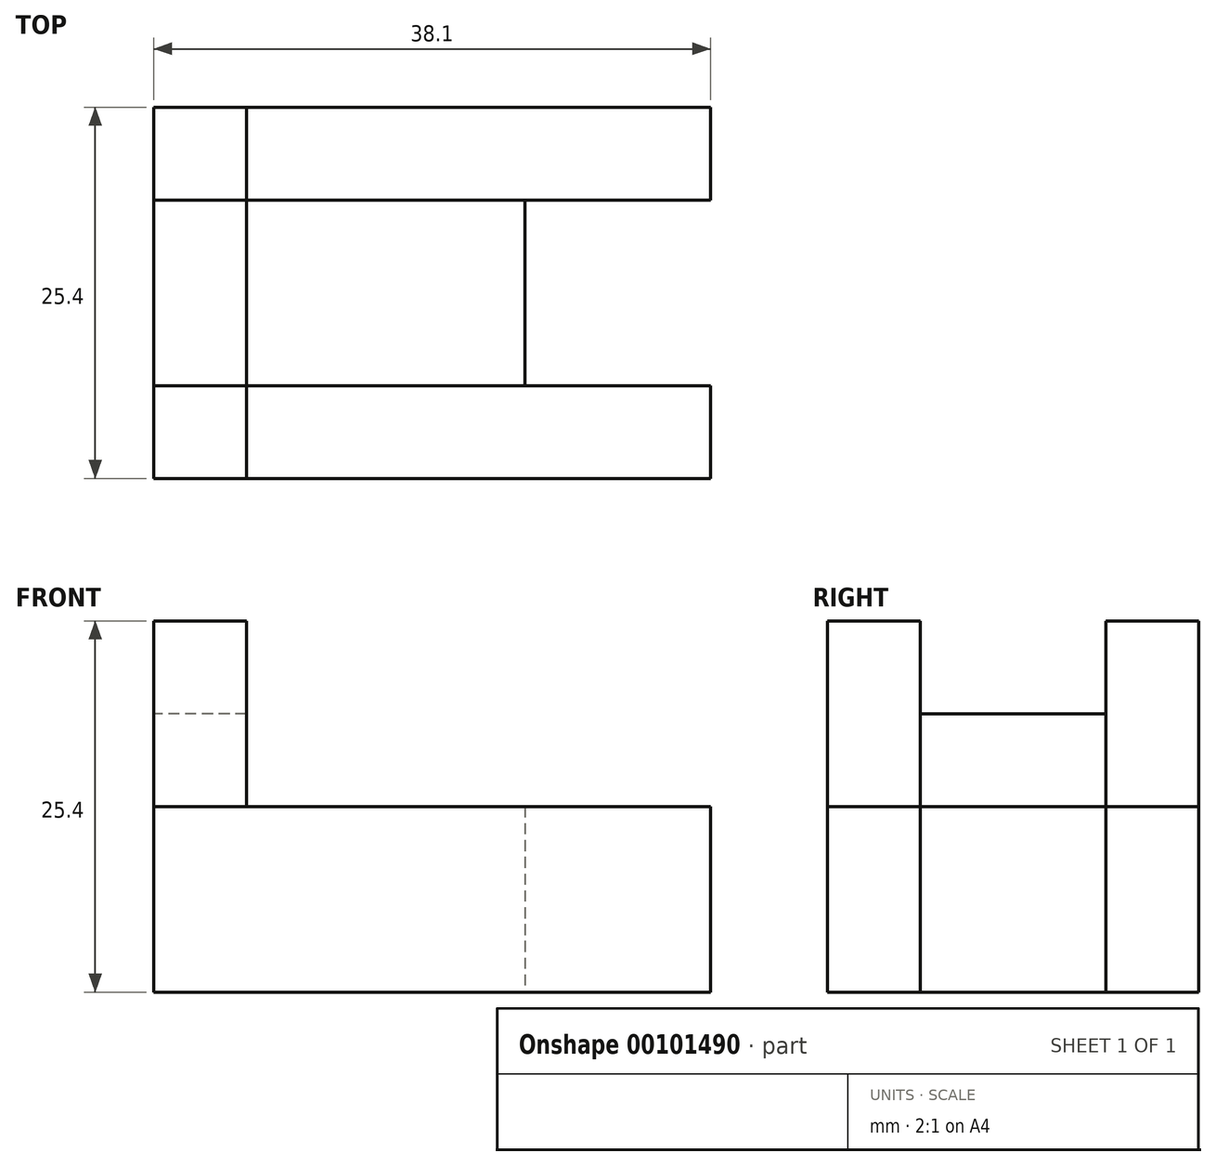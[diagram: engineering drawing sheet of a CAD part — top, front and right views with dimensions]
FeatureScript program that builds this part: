
annotation { "Feature Type Name" : "Feature", "Feature Type Description" : "" }
export const myFeature = defineFeature(function(context is Context, id is Id, definition is map)
    precondition{}
    {
        {
            var Q0;
            Q0=qCreatedBy(makeId("Right.planeOp"),FACE);
            var sketch = newSketch(context, id + "F0", { "sketchPlane" : qUnion([Q0])});
            skLineSegment(sketch, "E0", {"start": v(0, 0) * mm, "end": v(0, 12.7) * mm});
            skLineSegment(sketch, "E1", {"start": v(0, 12.7) * mm, "end": v(25.4, 12.7) * mm});
            skLineSegment(sketch, "E2", {"start": v(25.4, 12.7) * mm, "end": v(25.4, 0) * mm});
            skLineSegment(sketch, "E3", {"start": v(25.4, 0) * mm, "end": v(0, 0) * mm});
            skLineSegment(sketch, "E4", {"start": v(0, 12.7) * mm, "end": v(0, 25.4) * mm});
            skLineSegment(sketch, "E5", {"start": v(0, 25.4) * mm, "end": v(6.35, 25.4) * mm});
            skLineSegment(sketch, "E6", {"start": v(6.35, 25.4) * mm, "end": v(6.35, 12.7) * mm});
            skLineSegment(sketch, "E7", {"start": v(25.4, 12.7) * mm, "end": v(25.4, 25.4) * mm});
            skLineSegment(sketch, "E8", {"start": v(25.4, 25.4) * mm, "end": v(19.05, 25.4) * mm});
            skLineSegment(sketch, "E9", {"start": v(19.05, 25.4) * mm, "end": v(19.05, 12.7) * mm});
            skLineSegment(sketch, "E10", {"start": v(6.35, 12.7) * mm, "end": v(6.35, 0) * mm});
            skLineSegment(sketch, "E11", {"start": v(19.05, 12.7) * mm, "end": v(19.05, 0) * mm});
            skLineSegment(sketch, "E12", {"start": v(6.35, 19.05) * mm, "end": v(19.05, 19.05) * mm});
            skSolve(sketch);
        }
        {
            var Q0;
            {var subQ0=sQuery(id+"F0.wireOp",EDGE,"E0");Q0=makeQuery(id+"F0.imprint","IMPRINT",FACE,{"disambiguationData":[TD([[makeQuery(id+"F0.imprint","IMPRINT",EDGE,{"derivedFrom":subQ0}),-1.0]])]});}
            var Q1;
            {var subQ0=sQuery(id+"F0.wireOp",EDGE,"E2");Q1=makeQuery(id+"F0.imprint","IMPRINT",FACE,{"disambiguationData":[TD([[makeQuery(id+"F0.imprint","IMPRINT",EDGE,{"derivedFrom":subQ0}),-1.0]])]});}
            extrude(context, id + "F1", {"entities" : qUnion([Q0, Q1]), "depth" : 38.1 * mm});
        }
        {
            var Q0;
            {var subQ0=sQuery(id+"F0.wireOp",EDGE,"E10");Q0=makeQuery(id+"F0.imprint","IMPRINT",FACE,{"disambiguationData":[TD([[makeQuery(id+"F0.imprint","IMPRINT",EDGE,{"derivedFrom":subQ0}),1.0]])]});}
            extrude(context, id + "F2", {"entities" : qUnion([Q0]), "depth" : 25.4 * mm});
        }
        {
            var Q0;
            {var subQ0=sQuery(id+"F0.wireOp",EDGE,"E4");Q0=makeQuery(id+"F0.imprint","IMPRINT",FACE,{"disambiguationData":[TD([[makeQuery(id+"F0.imprint","IMPRINT",EDGE,{"derivedFrom":subQ0}),-1.0]])]});}
            var Q1;
            {var subQ0=sQuery(id+"F0.wireOp",EDGE,"E7");Q1=makeQuery(id+"F0.imprint","IMPRINT",FACE,{"disambiguationData":[TD([[makeQuery(id+"F0.imprint","IMPRINT",EDGE,{"derivedFrom":subQ0}),1.0]])]});}
            extrude(context, id + "F3", {"entities" : qUnion([Q0, Q1]), "depth" : 6.35 * mm});
        }
        {
            var Q0;
            {var subQ5=sQuery(id+"F0.wireOp",EDGE,"E12");Q0=makeQuery(id+"F0.imprint","IMPRINT",FACE,{"disambiguationData":[TD([[makeQuery(id+"F0.imprint","IMPRINT",EDGE,{"derivedFrom":subQ5}),-1.0]])]});}
            extrude(context, id + "F4", {"entities" : qUnion([Q0]), "depth" : 6.35 * mm});
        }
    });
